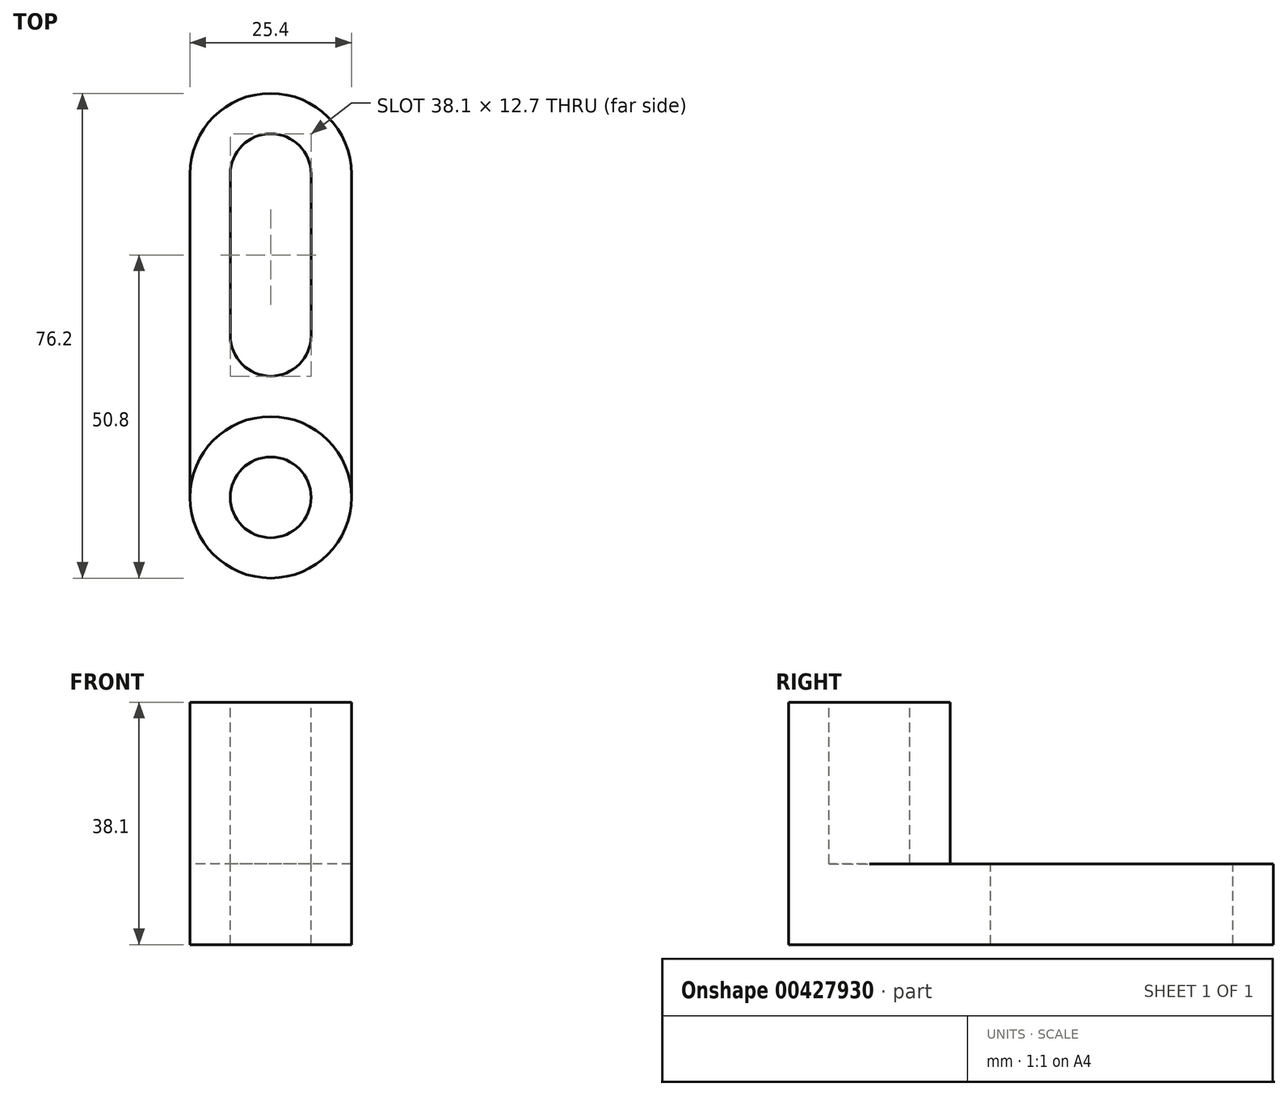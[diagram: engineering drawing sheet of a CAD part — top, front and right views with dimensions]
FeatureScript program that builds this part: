
annotation { "Feature Type Name" : "Feature", "Feature Type Description" : "" }
export const myFeature = defineFeature(function(context is Context, id is Id, definition is map)
    precondition{}
    {
        {
            var Q0;
            Q0=qCreatedBy(makeId("Right.planeOp"),FACE);
            var sketch = newSketch(context, id + "F0", { "sketchPlane" : qUnion([Q0])});
            skLineSegment(sketch, "E0", {"start": v(0, 0) * mm, "end": v(0, 38.1) * mm});
            skLineSegment(sketch, "E1", {"start": v(0, 38.1) * mm, "end": v(76.2, 38.1) * mm});
            skLineSegment(sketch, "E2", {"start": v(76.2, 38.1) * mm, "end": v(76.2, 0) * mm});
            skLineSegment(sketch, "E3", {"start": v(76.2, 0) * mm, "end": v(0, 0) * mm});
            skSolve(sketch);
        }
        {
            var Q0;
            Q0=makeQuery(id+"F0.imprint","IMPRINT",FACE,{"disambiguationData":[TD([[makeQuery(id+"F0.imprint","IMPRINT",EDGE,{"derivedFrom":sQuery(id+"F0.wireOp",EDGE,"E0")}),-1.0]])]});
            extrude(context, id + "F1", {"entities" : qUnion([Q0]), "depth" : 25.4 * mm});
        }
        {
            var Q0;
            Q0=makeQuery(id+"F1.opExtrude","CAP_FACE",FACE,{"disambiguationData":[OSD([sQuery(id+"F0.wireOp",EDGE,"E0"),sQuery(id+"F0.wireOp",EDGE,"E1"),sQuery(id+"F0.wireOp",EDGE,"E2"),sQuery(id+"F0.wireOp",EDGE,"E3")])],"isStart":false});
            var sketch = newSketch(context, id + "F2", { "sketchPlane" : qUnion([Q0])});
            skLineSegment(sketch, "E4", {"start": v(0, 38.1) * mm, "end": v(25.4, 38.1) * mm});
            skLineSegment(sketch, "E5", {"start": v(25.4, 38.1) * mm, "end": v(25.4, 12.7) * mm});
            skLineSegment(sketch, "E6", {"start": v(25.4, 12.7) * mm, "end": v(76.2, 12.7) * mm});
            skLineSegment(sketch, "E7", {"start": v(76.2, 12.7) * mm, "end": v(76.2, 0) * mm});
            skLineSegment(sketch, "E8", {"start": v(76.2, 0) * mm, "end": v(0, 0) * mm});
            skLineSegment(sketch, "E9", {"start": v(0, 0) * mm, "end": v(0, 38.1) * mm});
            skSolve(sketch);
        }
        {
            var Q0;
            {var subQ0=sQuery(id+"F2.wireOp",EDGE,"E5");Q0=makeQuery(id+"F2.imprint","IMPRINT",FACE,{"disambiguationData":[TD([[makeQuery(id+"F2.imprint","IMPRINT",EDGE,{"derivedFrom":subQ0}),1.0]])]});}
            extrude(context, id + "F3", {"entities" : qUnion([Q0]), "operationType" : NewBodyOperationType.REMOVE, "oppositeDirection" : true, "depth" : 25.4 * mm});
        }
        {
            var Q0;
            Q0=makeQuery(id+"F3.boolean.opBoolean","COPY",FACE,{"derivedFrom":makeQuery(id+"F3.opExtrude","SWEPT_FACE",FACE,{"disambiguationData":[OSD([sQuery(id+"F2.wireOp",EDGE,"E6")])]})});
            var sketch = newSketch(context, id + "F4", { "sketchPlane" : qUnion([Q0])});
            skArc(sketch, "E10", {"start": v(25.4, 63.5) * mm, "mid": v(12.7, 76.2) * mm, "end": v(0, 63.5) * mm});
            skCircle(sketch, "E11", {"center": v(12.7, 63.5) * mm, "radius": 6.35 * mm});
            skCircle(sketch, "E12", {"center": v(12.7, 38.1) * mm, "radius": 6.35 * mm});
            skLineSegment(sketch, "E13", {"start": v(6.35, 63.5) * mm, "end": v(6.35, 38.1) * mm});
            skLineSegment(sketch, "E14", {"start": v(6.35, 38.1) * mm, "end": v(12.7, 38.1) * mm});
            skLineSegment(sketch, "E15", {"start": v(19.05, 38.1) * mm, "end": v(19.05, 63.5) * mm});
            skLineSegment(sketch, "E16", {"start": v(19.05, 63.5) * mm, "end": v(12.7, 63.5) * mm});
            skSolve(sketch);
        }
        {
            var Q0;
            {var subQ0=sQuery(id+"F4.wireOp",EDGE,"E10");var subQ1=sQuery(id+"F2.wireOp",EDGE,"E6");var subQ2=makeQuery(id+"F3.boolean.opBoolean","COPY",EDGE,{"derivedFrom":makeQuery(id+"F3.opExtrude","CAP_EDGE",EDGE,{"disambiguationData":[OSD([subQ1])],"isStart":false})});var subQ3=makeQuery(id+"F4.imprint","INTERSECT",VERTEX,{"derivedFrom":[subQ2,subQ0]});Q0=makeQuery(id+"F4.imprint","IMPRINT",FACE,{"disambiguationData":[TD([[makeQuery(id+"F4.imprint","IMPRINT",EDGE,{"disambiguationData":[TD([[subQ3,1.0]])],"derivedFrom":subQ0}),-1.0]])]});}
            var Q1;
            {var subQ0=sQuery(id+"F4.wireOp",EDGE,"E10");var subQ1=sQuery(id+"F2.wireOp",EDGE,"E6");var subQ2=makeQuery(id+"F3.boolean.opBoolean","COPY",EDGE,{"derivedFrom":makeQuery(id+"F3.opExtrude","CAP_EDGE",EDGE,{"disambiguationData":[OSD([subQ1])],"isStart":true})});var subQ3=makeQuery(id+"F4.imprint","INTERSECT",VERTEX,{"derivedFrom":[subQ2,subQ0]});Q1=makeQuery(id+"F4.imprint","IMPRINT",FACE,{"disambiguationData":[TD([[makeQuery(id+"F4.imprint","IMPRINT",EDGE,{"disambiguationData":[TD([[subQ3,-1.0]])],"derivedFrom":subQ0}),-1.0]])]});}
            var Q2;
            {var subQ0=sQuery(id+"F4.wireOp",EDGE,"E11");var subQ1=makeQuery(id+"F4.imprint","INTERSECT",VERTEX,{"derivedFrom":[subQ0,sQuery(id+"F4.wireOp",EDGE,"E13")]});Q2=makeQuery(id+"F4.imprint","IMPRINT",FACE,{"disambiguationData":[TD([[makeQuery(id+"F4.imprint","IMPRINT",EDGE,{"disambiguationData":[TD([[subQ1,1.0]])],"derivedFrom":subQ0}),1.0]])]});}
            var Q3;
            {var subQ0=sQuery(id+"F4.wireOp",EDGE,"E13");Q3=makeQuery(id+"F4.imprint","IMPRINT",FACE,{"disambiguationData":[TD([[makeQuery(id+"F4.imprint","IMPRINT",EDGE,{"derivedFrom":subQ0}),1.0]])]});}
            var Q4;
            {var subQ0=sQuery(id+"F4.wireOp",EDGE,"E12");var subQ1=makeQuery(id+"F4.imprint","INTERSECT",VERTEX,{"derivedFrom":[subQ0,sQuery(id+"F4.wireOp",EDGE,"E13")]});Q4=makeQuery(id+"F4.imprint","IMPRINT",FACE,{"disambiguationData":[TD([[makeQuery(id+"F4.imprint","IMPRINT",EDGE,{"disambiguationData":[TD([[subQ1,1.0]])],"derivedFrom":subQ0}),1.0]])]});}
            extrude(context, id + "F5", {"entities" : qUnion([Q0, Q1, Q2, Q3, Q4]), "operationType" : NewBodyOperationType.REMOVE, "oppositeDirection" : true, "depth" : 12.7 * mm});
        }
        {
            var Q0;
            Q0=makeQuery(id+"F1.opExtrude","SWEPT_FACE",FACE,{"disambiguationData":[OSD([sQuery(id+"F0.wireOp",EDGE,"E1")])]});
            var sketch = newSketch(context, id + "F6", { "sketchPlane" : qUnion([Q0])});
            skCircle(sketch, "E17", {"center": v(12.7, 12.7) * mm, "radius": 6.35 * mm});
            skPoint(sketch, "E17.centerSnap0", {"position": v(25.4, 12.7) * mm});
            skCircle(sketch, "E18", {"center": v(12.7, 12.7) * mm, "radius": 12.7 * mm});
            skSolve(sketch);
        }
        {
            var Q0;
            Q0=makeQuery(id+"F6.imprint","IMPRINT",FACE,{"disambiguationData":[TD([[makeQuery(id+"F6.imprint","IMPRINT",EDGE,{"derivedFrom":sQuery(id+"F6.wireOp",EDGE,"E17")}),1.0]])]});
            var Q1;
            {var subQ0=sQuery(id+"F6.wireOp",EDGE,"E18");var subQ1=sQuery(id+"F0.wireOp",EDGE,"E1");var subQ4=makeQuery(id+"F1.opExtrude","CAP_EDGE",EDGE,{"disambiguationData":[OSD([subQ1])],"isStart":false});var subQ5=makeQuery(id+"F6.imprint","INTERSECT",VERTEX,{"derivedFrom":[subQ4,subQ0]});Q1=makeQuery(id+"F6.imprint","IMPRINT",FACE,{"disambiguationData":[TD([[makeQuery(id+"F6.imprint","IMPRINT",EDGE,{"disambiguationData":[TD([[subQ5,-1.0]])],"derivedFrom":subQ0}),-1.0]])]});}
            var Q2;
            {var subQ0=sQuery(id+"F6.wireOp",EDGE,"E18");var subQ1=sQuery(id+"F0.wireOp",EDGE,"E1");var subQ4=makeQuery(id+"F1.opExtrude","CAP_EDGE",EDGE,{"disambiguationData":[OSD([subQ1])],"isStart":true});var subQ5=makeQuery(id+"F6.imprint","INTERSECT",VERTEX,{"derivedFrom":[subQ4,subQ0]});Q2=makeQuery(id+"F6.imprint","IMPRINT",FACE,{"disambiguationData":[TD([[makeQuery(id+"F6.imprint","IMPRINT",EDGE,{"disambiguationData":[TD([[subQ5,1.0]])],"derivedFrom":subQ0}),-1.0]])]});}
            var Q3;
            {var subQ0=sQuery(id+"F6.wireOp",EDGE,"E18");var subQ1=sQuery(id+"F0.wireOp",EDGE,"E1");var subQ2=makeQuery(id+"F1.opExtrude","CAP_EDGE",EDGE,{"disambiguationData":[OSD([subQ1])],"isStart":true});var subQ3=makeQuery(id+"F6.imprint","INTERSECT",VERTEX,{"derivedFrom":[subQ2,subQ0]});Q3=makeQuery(id+"F6.imprint","IMPRINT",FACE,{"disambiguationData":[TD([[makeQuery(id+"F6.imprint","IMPRINT",EDGE,{"disambiguationData":[TD([[subQ3,-1.0]])],"derivedFrom":subQ0}),-1.0]])]});}
            var Q4;
            {var subQ0=sQuery(id+"F6.wireOp",EDGE,"E18");var subQ1=sQuery(id+"F0.wireOp",EDGE,"E1");var subQ2=makeQuery(id+"F1.opExtrude","CAP_EDGE",EDGE,{"disambiguationData":[OSD([subQ1])],"isStart":false});var subQ3=makeQuery(id+"F6.imprint","INTERSECT",VERTEX,{"derivedFrom":[subQ2,subQ0]});Q4=makeQuery(id+"F6.imprint","IMPRINT",FACE,{"disambiguationData":[TD([[makeQuery(id+"F6.imprint","IMPRINT",EDGE,{"disambiguationData":[TD([[subQ3,1.0]])],"derivedFrom":subQ0}),-1.0]])]});}
            extrude(context, id + "F7", {"entities" : qUnion([Q0, Q1, Q2, Q3, Q4]), "operationType" : NewBodyOperationType.REMOVE, "oppositeDirection" : true, "depth" : 25.4 * mm});
        }
        {
            var Q0;
            {var subQ0=sQuery(id+"F0.wireOp",EDGE,"E1");var subQ1=makeQuery(id+"F1.opExtrude","CAP_EDGE",EDGE,{"disambiguationData":[OSD([subQ0])],"isStart":false});var subQ2=sQuery(id+"F0.wireOp",EDGE,"E0");var subQ3=makeQuery(id+"F1.opExtrude","SWEPT_EDGE",EDGE,{"disambiguationData":[OSD([subQ2,subQ0])]});var subQ4=makeQuery(id+"F6.imprint","INTERSECT",VERTEX,{"derivedFrom":[subQ3,subQ1]});var subQ5=sQuery(id+"F6.wireOp",EDGE,"E18");var subQ6=makeQuery(id+"F6.imprint","INTERSECT",VERTEX,{"derivedFrom":[subQ1,subQ5]});Q0=makeQuery(id+"F7.boolean.opBoolean","COPY",FACE,{"derivedFrom":makeQuery(id+"F7.opExtrude","CAP_FACE",FACE,{"disambiguationData":[OSD([subQ2,subQ0,subQ5]),TDD([makeQuery(id+"F6.imprint","IMPRINT",EDGE,{"disambiguationData":[TD([[subQ6,1.0]])],"derivedFrom":subQ5}),makeQuery(id+"F6.imprint","IMPRINT",EDGE,{"disambiguationData":[TD([[subQ4,-1.0]])],"derivedFrom":subQ3}),makeQuery(id+"F6.imprint","IMPRINT",EDGE,{"disambiguationData":[TD([[subQ6,1.0]])],"derivedFrom":subQ1})])],"isStart":false})});}
            var Q1;
            {var subQ0=sQuery(id+"F0.wireOp",EDGE,"E1");var subQ1=makeQuery(id+"F1.opExtrude","CAP_EDGE",EDGE,{"disambiguationData":[OSD([subQ0])],"isStart":true});var subQ2=sQuery(id+"F0.wireOp",EDGE,"E0");var subQ3=makeQuery(id+"F1.opExtrude","SWEPT_EDGE",EDGE,{"disambiguationData":[OSD([subQ2,subQ0])]});var subQ4=makeQuery(id+"F6.imprint","INTERSECT",VERTEX,{"derivedFrom":[subQ3,subQ1]});var subQ5=sQuery(id+"F6.wireOp",EDGE,"E18");var subQ6=makeQuery(id+"F6.imprint","INTERSECT",VERTEX,{"derivedFrom":[subQ1,subQ5]});Q1=makeQuery(id+"F7.boolean.opBoolean","COPY",FACE,{"derivedFrom":makeQuery(id+"F7.opExtrude","CAP_FACE",FACE,{"disambiguationData":[OSD([subQ2,subQ0,subQ5]),TDD([makeQuery(id+"F6.imprint","IMPRINT",EDGE,{"disambiguationData":[TD([[subQ6,-1.0]])],"derivedFrom":subQ5}),makeQuery(id+"F6.imprint","IMPRINT",EDGE,{"disambiguationData":[TD([[subQ4,1.0]])],"derivedFrom":subQ3}),makeQuery(id+"F6.imprint","IMPRINT",EDGE,{"disambiguationData":[TD([[subQ6,1.0]])],"derivedFrom":subQ1})])],"isStart":false})});}
            extrude(context, id + "F8", {"entities" : qUnion([Q0, Q1]), "operationType" : NewBodyOperationType.REMOVE, "oppositeDirection" : true, "depth" : 25.4 * mm});
        }
    });
